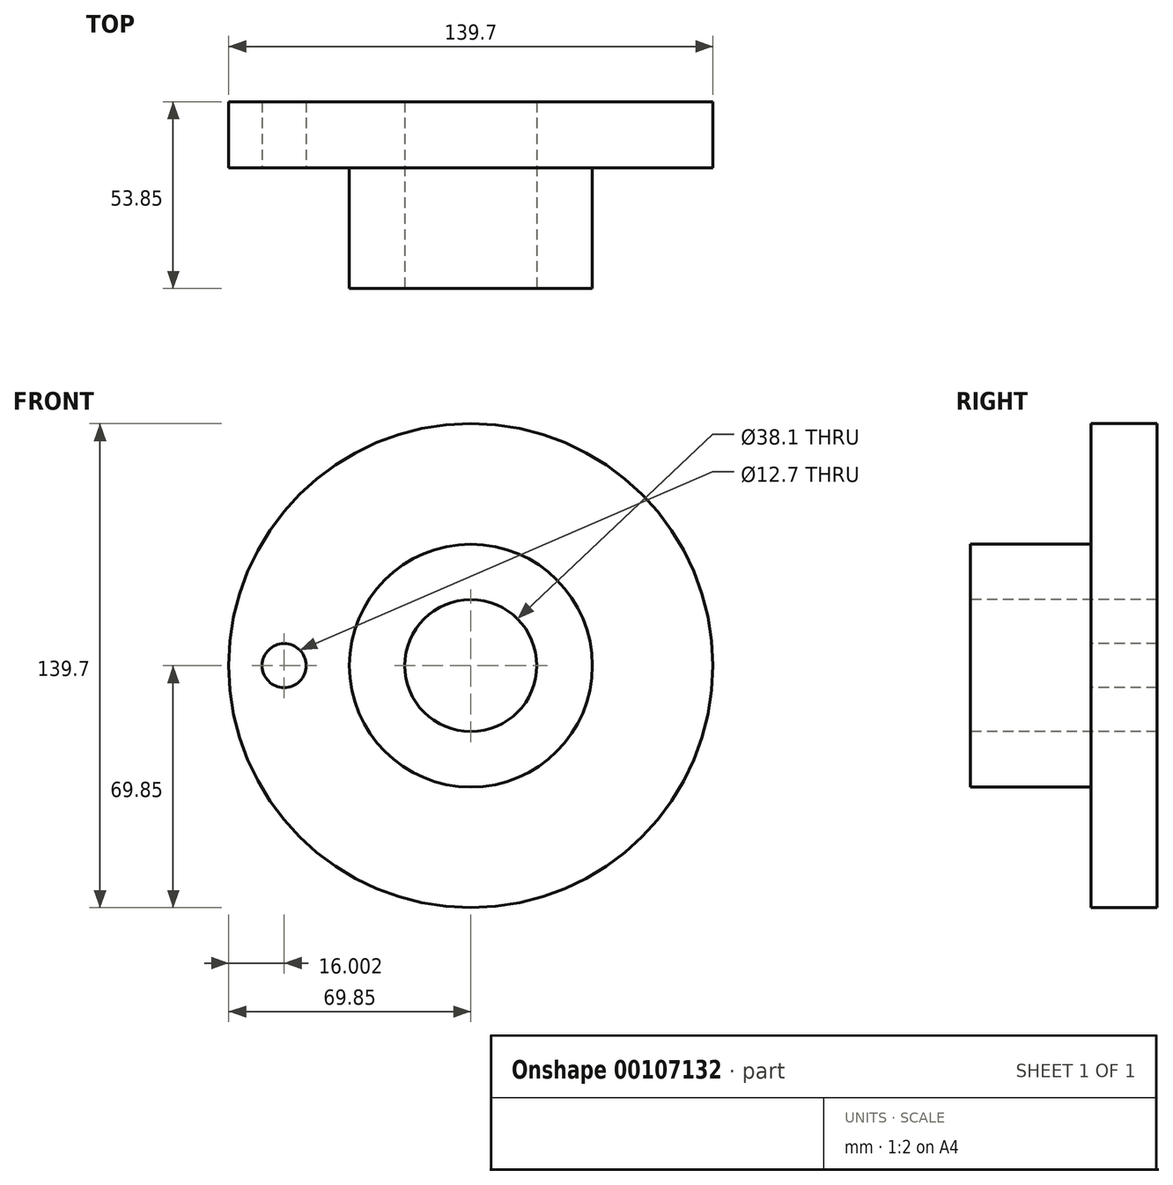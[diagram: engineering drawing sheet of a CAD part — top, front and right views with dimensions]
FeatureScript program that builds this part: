
annotation { "Feature Type Name" : "Feature", "Feature Type Description" : "" }
export const myFeature = defineFeature(function(context is Context, id is Id, definition is map)
    precondition{}
    {
        {
            var Q0;
            Q0=qCreatedBy(makeId("Right.planeOp"),FACE);
            var sketch = newSketch(context, id + "F0", { "sketchPlane" : qUnion([Q0])});
            skLineSegment(sketch, "E0", {"start": v(0, 0) * mm, "end": v(106.3, 0) * mm, "construction": true});
            skLineSegment(sketch, "E1", {"start": v(0, 35.05) * mm, "end": v(0, 19.05) * mm});
            skLineSegment(sketch, "E2", {"start": v(0, 19.05) * mm, "end": v(53.85, 19.05) * mm});
            skLineSegment(sketch, "E3", {"start": v(53.85, 19.05) * mm, "end": v(53.85, 69.85) * mm});
            skLineSegment(sketch, "E4", {"start": v(53.85, 69.85) * mm, "end": v(34.8, 69.85) * mm});
            skLineSegment(sketch, "E5", {"start": v(34.8, 69.85) * mm, "end": v(34.8, 35.05) * mm});
            skLineSegment(sketch, "E6", {"start": v(34.8, 35.05) * mm, "end": v(0, 35.05) * mm});
            skSolve(sketch);
        }
        {
            var Q0;
            Q0 = qSketchRegion(id + "F0", true);
            var Q1;
            Q1=sQuery(id+"F0.wireOp",EDGE,"E0");
            revolve(context, id + "F1", {"entities" : qUnion([Q0]), "axis" : qUnion([Q1]), "revolveType" : RevolveType.FULL});
        }
        {
            var Q0;
            Q0=qCreatedBy(makeId("Front.planeOp"),FACE);
            var sketch = newSketch(context, id + "F2", { "sketchPlane" : qUnion([Q0])});
            skLineSegment(sketch, "E7", {"start": v(0, 0) * mm, "end": v(0, 64.46) * mm, "construction": true});
            skCircle(sketch, "E8", {"center": v(-53.85, 0) * mm, "radius": 6.35 * mm});
            skCircle(sketch, "E9", {"center": v(0, 0) * mm, "radius": 53.85 * mm, "construction": true});
            skCircle(sketch, "E10", {"center": v(0, 53.85) * mm, "radius": 6.35 * mm});
            skCircle(sketch, "E11", {"center": v(53.85, 0) * mm, "radius": 6.35 * mm});
            skCircle(sketch, "E12", {"center": v(0, -53.85) * mm, "radius": 6.35 * mm});
            skSolve(sketch);
        }
        {
            var Q0;
            Q0=makeQuery(id+"F2.imprint","IMPRINT",FACE,{"disambiguationData":[TD([[makeQuery(id+"F2.imprint","IMPRINT",EDGE,{"derivedFrom":sQuery(id+"F2.wireOp",EDGE,"E8")}),1.0]])]});
            extrude(context, id + "F3", {"entities" : qUnion([Q0]), "operationType" : NewBodyOperationType.REMOVE, "endBound" : BoundingType.THROUGH_ALL, "oppositeDirection" : true, "depth" : 25.4 * mm});
        }
    });
